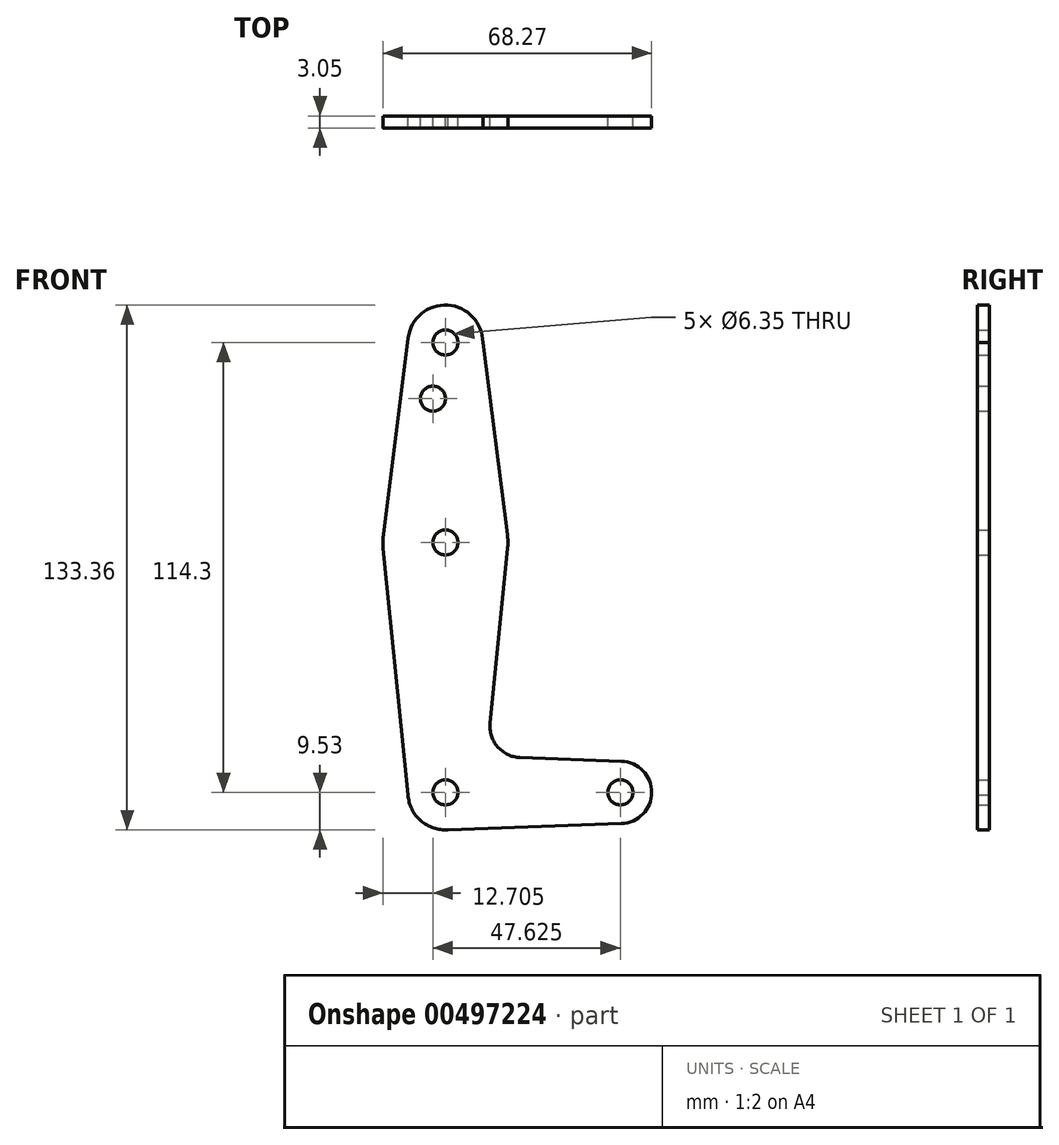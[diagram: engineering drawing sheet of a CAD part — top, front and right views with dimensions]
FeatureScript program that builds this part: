
annotation { "Feature Type Name" : "Feature", "Feature Type Description" : "" }
export const myFeature = defineFeature(function(context is Context, id is Id, definition is map)
    precondition{}
    {
        {
            var Q0;
            Q0=qCreatedBy(makeId("Front.planeOp"),FACE);
            var sketch = newSketch(context, id + "F0", { "sketchPlane" : qUnion([Q0])});
            skLineSegment(sketch, "E0", {"start": v(0, 0) * mm, "end": v(0, 114.3) * mm, "construction": true});
            skCircle(sketch, "E1", {"center": v(0, 114.3) * mm, "radius": 9.53 * mm});
            skCircle(sketch, "E2", {"center": v(0, 0) * mm, "radius": 9.53 * mm});
            skLineSegment(sketch, "E3", {"start": v(0, 0) * mm, "end": v(44.45, 0) * mm, "construction": true});
            skCircle(sketch, "E4", {"center": v(44.45, 0) * mm, "radius": 7.94 * mm});
            skCircle(sketch, "E5", {"center": v(0, 63.5) * mm, "radius": 15.88 * mm});
            skLineSegment(sketch, "E6", {"start": v(-9.45, 115.5) * mm, "end": v(-15.75, 65.48) * mm});
            skLineSegment(sketch, "E7", {"start": v(9.53, 114.3) * mm, "end": v(15.75, 65.5) * mm});
            skLineSegment(sketch, "E8", {"start": v(18.96, 8.86) * mm, "end": v(44.74, 7.93) * mm});
            skLineSegment(sketch, "E9", {"start": v(0, -9.53) * mm, "end": v(44.73, -7.93) * mm});
            skLineSegment(sketch, "E10", {"start": v(15.8, 61.91) * mm, "end": v(11.34, 17.6) * mm});
            skLineSegment(sketch, "E11", {"start": v(-15.8, 61.91) * mm, "end": v(-9.44, -1.27) * mm});
            skCircle(sketch, "E12", {"center": v(0, 114.3) * mm, "radius": 3.18 * mm});
            skCircle(sketch, "E13", {"center": v(0, 63.5) * mm, "radius": 3.18 * mm});
            skCircle(sketch, "E14", {"center": v(0, 0) * mm, "radius": 3.18 * mm});
            skCircle(sketch, "E15", {"center": v(44.45, 0) * mm, "radius": 3.18 * mm});
            skCircle(sketch, "E16", {"center": v(-3.18, 100.03) * mm, "radius": 3.18 * mm});
            skPoint(sketch, "E17.newPointA", {"position": v(9.44, -1.27) * mm});
            skPoint(sketch, "E17.newPointB", {"position": v(0, 9.55) * mm});
            skArc(sketch, "E17.filletArc", {"start": v(11.34, 17.6) * mm, "mid": v(13.26, 11.58) * mm, "end": v(18.96, 8.86) * mm});
            skSolve(sketch);
        }
        {
            var Q0;
            Q0 = qSketchRegion(id + "F0", true);
            extrude(context, id + "F1", {"entities" : qUnion([Q0]), "depth" : 3.05 * mm});
        }
    });
